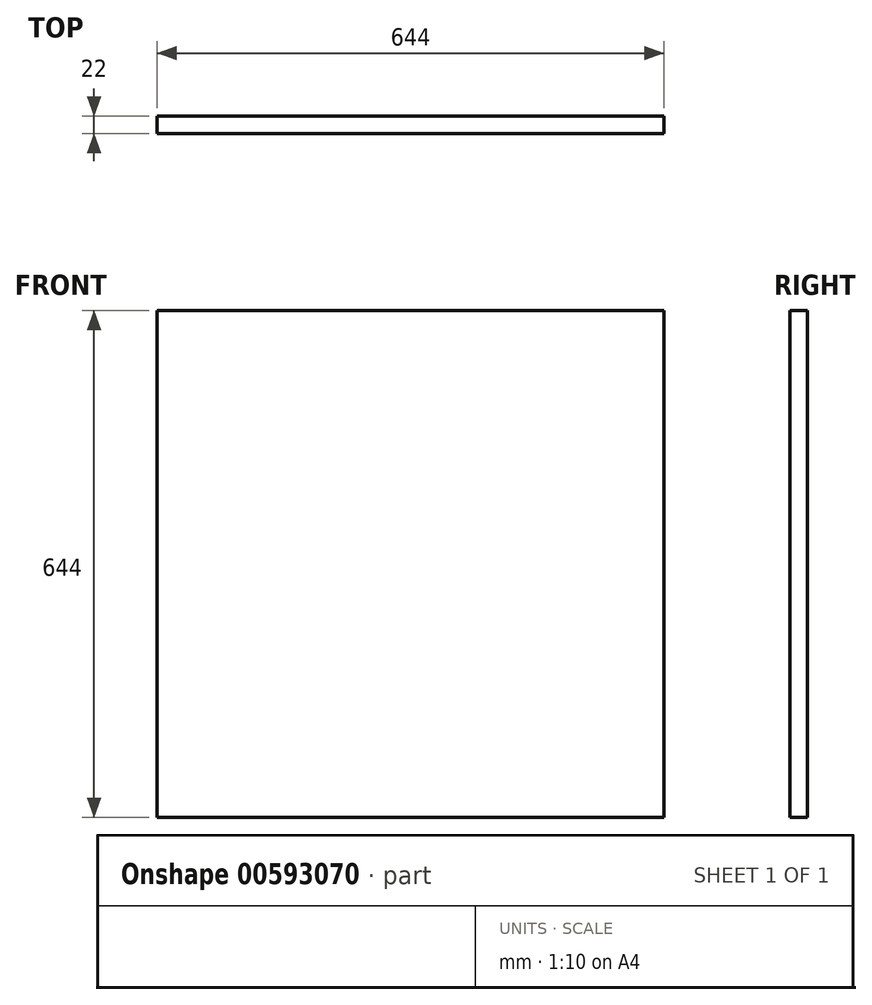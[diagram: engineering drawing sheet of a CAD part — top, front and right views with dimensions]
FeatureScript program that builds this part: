
annotation { "Feature Type Name" : "Feature", "Feature Type Description" : "" }
export const myFeature = defineFeature(function(context is Context, id is Id, definition is map)
    precondition{}
    {
        {
            var Q0;
            Q0=qCreatedBy(makeId("Front.planeOp"),FACE);
            var sketch = newSketch(context, id + "F0", { "sketchPlane" : qUnion([Q0])});
            skLineSegment(sketch, "E0.bottom", {"start": v(-322, 322) * mm, "end": v(322, 322) * mm});
            skLineSegment(sketch, "E0.top", {"start": v(-322, -322) * mm, "end": v(322, -322) * mm});
            skLineSegment(sketch, "E0.left", {"start": v(-322, 322) * mm, "end": v(-322, -322) * mm});
            skLineSegment(sketch, "E0.right", {"start": v(322, 322) * mm, "end": v(322, -322) * mm});
            skSolve(sketch);
        }
        {
            var Q0;
            Q0=makeQuery(id+"F0.imprint","IMPRINT",FACE,{"disambiguationData":[TD([[makeQuery(id+"F0.imprint","IMPRINT",EDGE,{"derivedFrom":sQuery(id+"F0.wireOp",EDGE,"E0.bottom")}),-1.0]])]});
            extrude(context, id + "F1", {"entities" : qUnion([Q0]), "depth" : 22 * mm, "offsetDistance" : 25 * mm});
        }
    });
